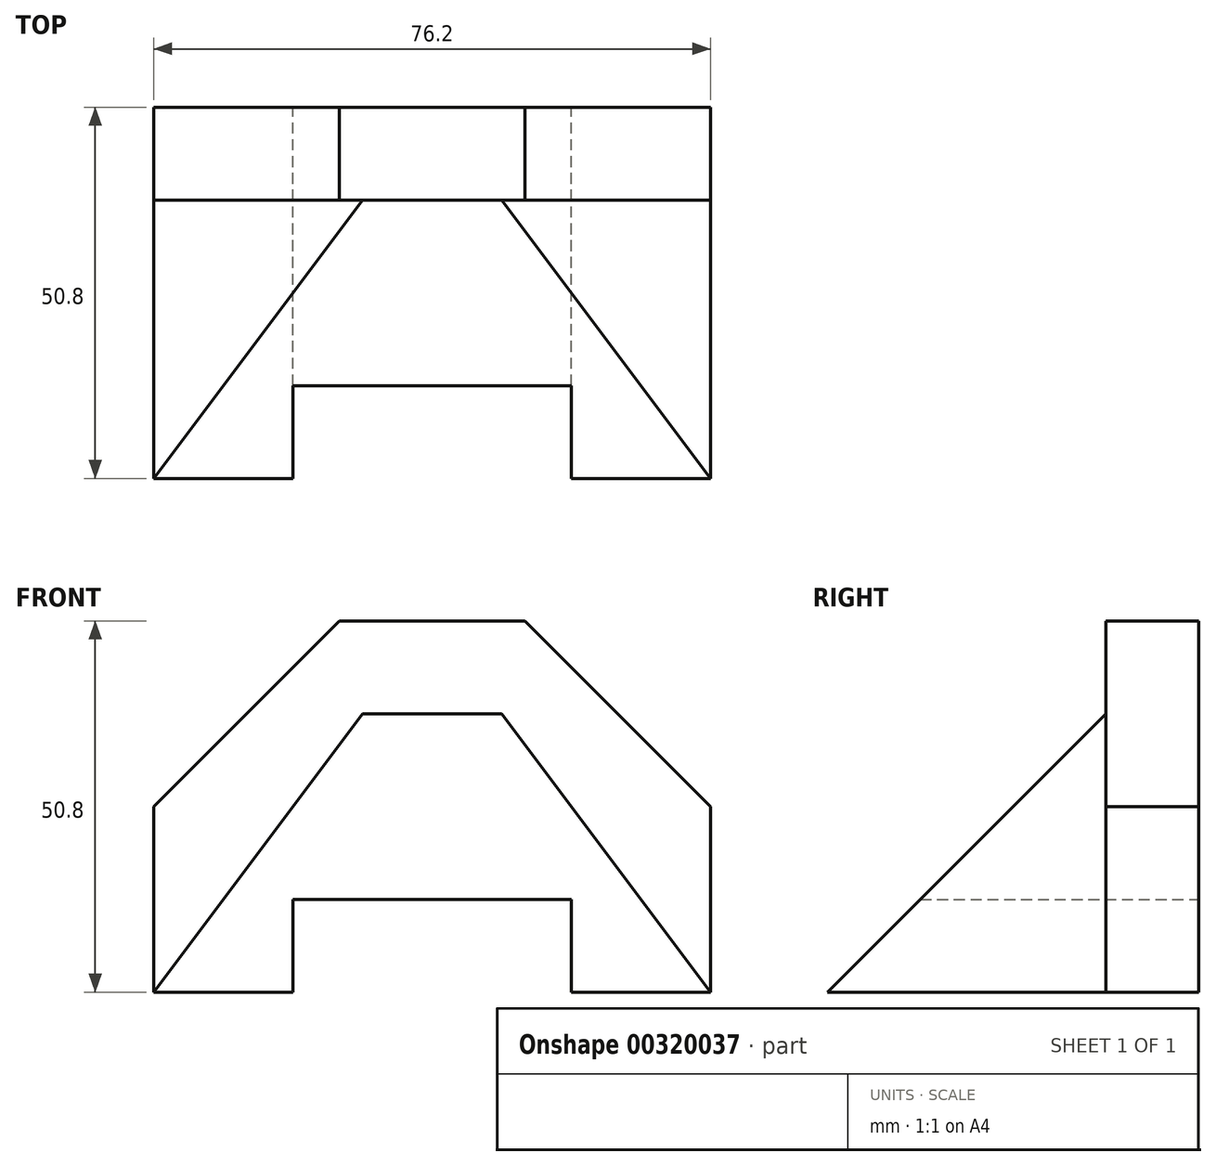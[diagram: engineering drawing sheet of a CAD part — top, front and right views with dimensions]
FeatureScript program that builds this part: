
annotation { "Feature Type Name" : "Feature", "Feature Type Description" : "" }
export const myFeature = defineFeature(function(context is Context, id is Id, definition is map)
    precondition{}
    {
        {
            var Q0;
            Q0=qCreatedBy(makeId("Front.planeOp"),FACE);
            var sketch = newSketch(context, id + "F0", { "sketchPlane" : qUnion([Q0])});
            skLineSegment(sketch, "E0", {"start": v(0, 0) * mm, "end": v(0, 25.4) * mm});
            skLineSegment(sketch, "E1", {"start": v(0, 25.4) * mm, "end": v(25.4, 50.8) * mm});
            skLineSegment(sketch, "E2", {"start": v(25.4, 50.8) * mm, "end": v(50.8, 50.8) * mm});
            skLineSegment(sketch, "E3", {"start": v(50.8, 50.8) * mm, "end": v(76.2, 25.4) * mm});
            skLineSegment(sketch, "E4", {"start": v(76.2, 25.4) * mm, "end": v(76.2, 0) * mm});
            skLineSegment(sketch, "E5", {"start": v(76.2, 0) * mm, "end": v(0, 0) * mm});
            skSolve(sketch);
        }
        {
            var Q0;
            Q0 = qSketchRegion(id + "F0", true);
            extrude(context, id + "F1", {"entities" : qUnion([Q0]), "depth" : 12.7 * mm});
        }
        {
            var Q0;
            Q0=makeQuery(id+"F1.opExtrude","CAP_FACE",FACE,{"disambiguationData":[OSD([sQuery(id+"F0.wireOp",EDGE,"E0"),sQuery(id+"F0.wireOp",EDGE,"E1"),sQuery(id+"F0.wireOp",EDGE,"E2"),sQuery(id+"F0.wireOp",EDGE,"E3"),sQuery(id+"F0.wireOp",EDGE,"E4"),sQuery(id+"F0.wireOp",EDGE,"E5")])],"isStart":false});
            var sketch = newSketch(context, id + "F2", { "sketchPlane" : qUnion([Q0])});
            skLineSegment(sketch, "E6", {"start": v(0, 0) * mm, "end": v(38.1, 50.8) * mm});
            skLineSegment(sketch, "E7", {"start": v(38.1, 50.8) * mm, "end": v(76.2, 0) * mm});
            skLineSegment(sketch, "E8", {"start": v(0, 0) * mm, "end": v(76.2, 0) * mm});
            skSolve(sketch);
        }
        {
            var Q0;
            Q0 = qSketchRegion(id + "F2", true);
            extrude(context, id + "F3", {"entities" : qUnion([Q0]), "operationType" : NewBodyOperationType.ADD, "depth" : 38.1 * mm});
        }
        {
            var Q0;
            Q0=makeQuery(id+"F1.opExtrude","CAP_FACE",FACE,{"disambiguationData":[OSD([sQuery(id+"F0.wireOp",EDGE,"E0"),sQuery(id+"F0.wireOp",EDGE,"E1"),sQuery(id+"F0.wireOp",EDGE,"E2"),sQuery(id+"F0.wireOp",EDGE,"E3"),sQuery(id+"F0.wireOp",EDGE,"E4"),sQuery(id+"F0.wireOp",EDGE,"E5")])],"isStart":true});
            var sketch = newSketch(context, id + "F4", { "sketchPlane" : qUnion([Q0])});
            skLineSegment(sketch, "E9", {"start": v(-57.15, 0) * mm, "end": v(-57.15, 12.7) * mm});
            skLineSegment(sketch, "E10", {"start": v(-57.15, 12.7) * mm, "end": v(-19.05, 12.7) * mm});
            skLineSegment(sketch, "E11", {"start": v(-19.05, 12.7) * mm, "end": v(-19.05, 0) * mm});
            skLineSegment(sketch, "E12", {"start": v(-57.15, 0) * mm, "end": v(-19.05, 0) * mm});
            skLineSegment(sketch, "E13", {"start": v(-19.05, 7.58) * mm, "end": v(0, 7.58) * mm, "construction": true});
            skLineSegment(sketch, "E14", {"start": v(-57.15, 6.35) * mm, "end": v(-76.2, 6.35) * mm, "construction": true});
            skSolve(sketch);
        }
        {
            var Q0;
            Q0=makeQuery(id+"F4.imprint","IMPRINT",FACE,{"disambiguationData":[TD([[makeQuery(id+"F4.imprint","IMPRINT",EDGE,{"derivedFrom":sQuery(id+"F4.wireOp",EDGE,"E9")}),-1.0]])]});
            extrude(context, id + "F5", {"entities" : qUnion([Q0]), "operationType" : NewBodyOperationType.REMOVE, "endBound" : BoundingType.THROUGH_ALL, "oppositeDirection" : true, "depth" : 25.4 * mm});
        }
        {
            var Q0;
            Q0=makeQuery(id+"F1.opExtrude","SWEPT_FACE",FACE,{"disambiguationData":[OSD([sQuery(id+"F0.wireOp",EDGE,"E4")])]});
            var sketch = newSketch(context, id + "F6", { "sketchPlane" : qUnion([Q0])});
            skLineSegment(sketch, "E15", {"start": v(0, 0) * mm, "end": v(0, 50.8) * mm, "construction": true});
            skLineSegment(sketch, "E16", {"start": v(0, 50.8) * mm, "end": v(-12.7, 50.8) * mm, "construction": true});
            skLineSegment(sketch, "E17", {"start": v(-50.8, 0) * mm, "end": v(0, 0) * mm, "construction": true});
            skLineSegment(sketch, "E18", {"start": v(-12.7, 50.8) * mm, "end": v(-50.8, 50.8) * mm});
            skLineSegment(sketch, "E19", {"start": v(-50.8, 50.8) * mm, "end": v(-50.8, 0) * mm});
            skLineSegment(sketch, "E20", {"start": v(-12.7, 50.8) * mm, "end": v(-12.7, 38.1) * mm});
            skLineSegment(sketch, "E21", {"start": v(-12.7, 38.1) * mm, "end": v(-50.8, 0) * mm});
            skSolve(sketch);
        }
        {
            var Q0;
            Q0 = qSketchRegion(id + "F6", true);
            extrude(context, id + "F7", {"entities" : qUnion([Q0]), "operationType" : NewBodyOperationType.REMOVE, "endBound" : BoundingType.THROUGH_ALL, "oppositeDirection" : true, "depth" : 25.4 * mm});
        }
    });
